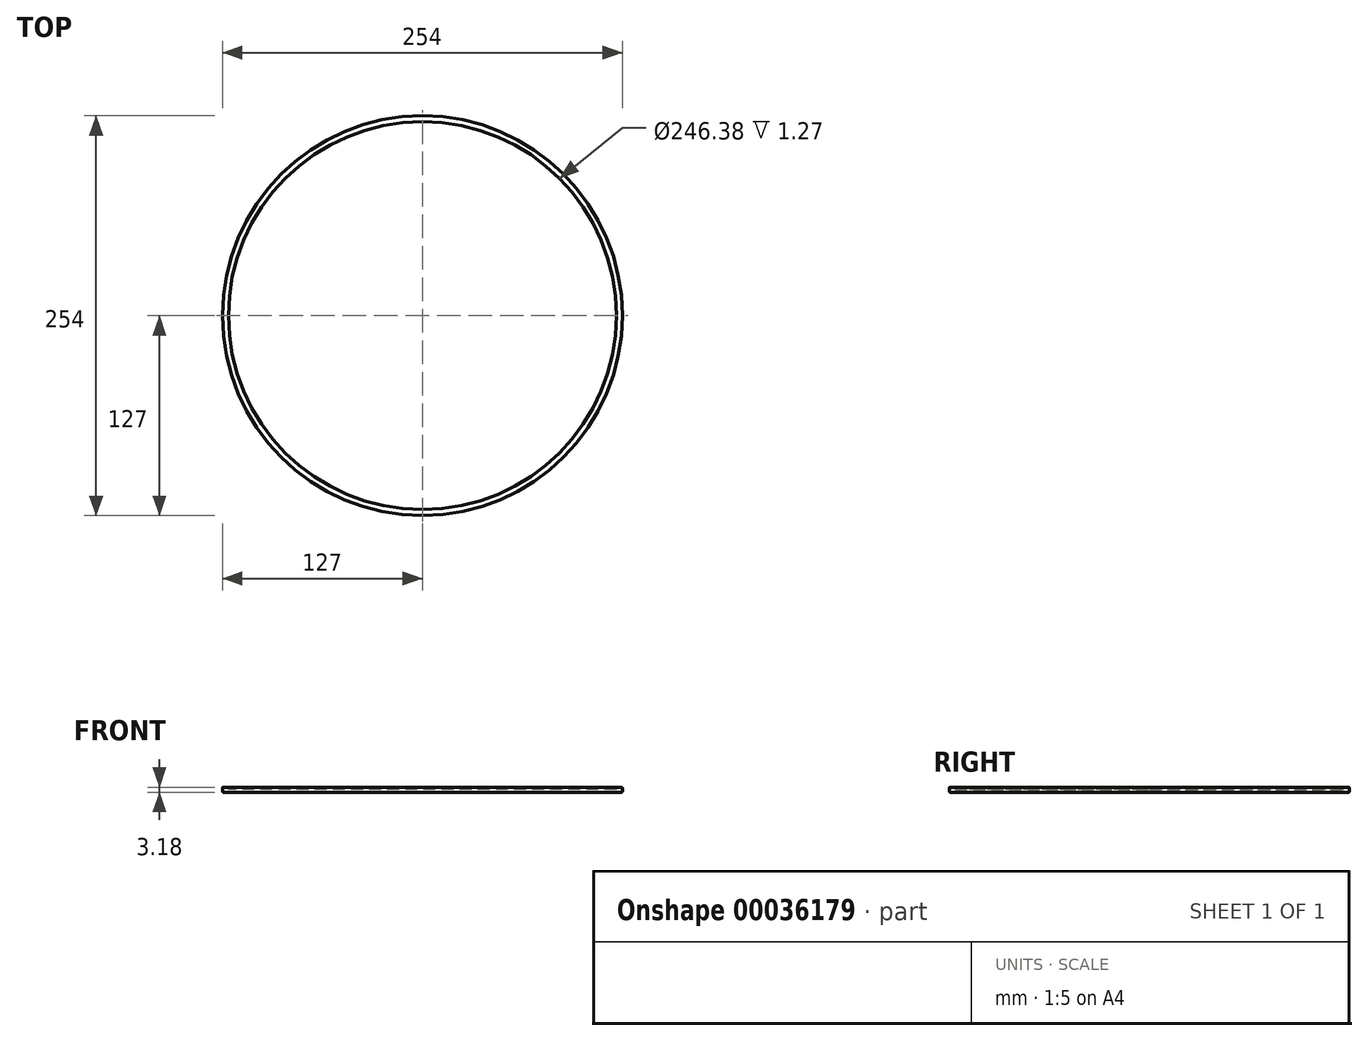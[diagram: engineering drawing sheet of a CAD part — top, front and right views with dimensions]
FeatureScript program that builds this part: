
annotation { "Feature Type Name" : "Feature", "Feature Type Description" : "" }
export const myFeature = defineFeature(function(context is Context, id is Id, definition is map)
    precondition{}
    {
        {
            var Q0;
            Q0=qCreatedBy(makeId("Top.planeOp"),FACE);
            var sketch = newSketch(context, id + "F0", { "sketchPlane" : qUnion([Q0])});
            skCircle(sketch, "E0", {"center": v(0, 0) * mm, "radius": 127 * mm});
            skSolve(sketch);
        }
        {
            var Q0;
            Q0=makeQuery(id+"F0.imprint","IMPRINT",FACE,{"disambiguationData":[TD([[makeQuery(id+"F0.imprint","IMPRINT",EDGE,{"derivedFrom":sQuery(id+"F0.wireOp",EDGE,"E0")}),1.0]])]});
            extrude(context, id + "F1", {"entities" : qUnion([Q0]), "depth" : 3.17 * mm});
        }
        {
            var Q0;
            Q0=makeQuery(id+"F1.opExtrude","CAP_EDGE",EDGE,{"disambiguationData":[OSD([sQuery(id+"F0.wireOp",EDGE,"E0")])],"isStart":true});
            var Q1;
            Q1=makeQuery(id+"F1.opExtrude","CAP_EDGE",EDGE,{"disambiguationData":[OSD([sQuery(id+"F0.wireOp",EDGE,"E0")])],"isStart":false});
            fillet(context, id + "F2", {"entities" : qUnion([Q0, Q1]), "radius" : 0.5 * mm, "tangentPropagation" : true, "allowEdgeOverflow" : false});
        }
        {
            var Q0;
            Q0=makeQuery(id+"F1.opExtrude","CAP_FACE",FACE,{"disambiguationData":[OSD([sQuery(id+"F0.wireOp",EDGE,"E0")])],"isStart":false});
            var sketch = newSketch(context, id + "F3", { "sketchPlane" : qUnion([Q0])});
            skCircle(sketch, "E1", {"center": v(0, 0) * mm, "radius": 123.2 * mm});
            skSolve(sketch);
        }
        {
            var Q0;
            Q0=makeQuery(id+"F3.imprint","IMPRINT",FACE,{"disambiguationData":[TD([[makeQuery(id+"F3.imprint","IMPRINT",EDGE,{"derivedFrom":sQuery(id+"F3.wireOp",EDGE,"E1")}),1.0]])]});
            extrude(context, id + "F4", {"entities" : qUnion([Q0]), "operationType" : NewBodyOperationType.REMOVE, "oppositeDirection" : true, "depth" : 1.27 * mm});
        }
    });
